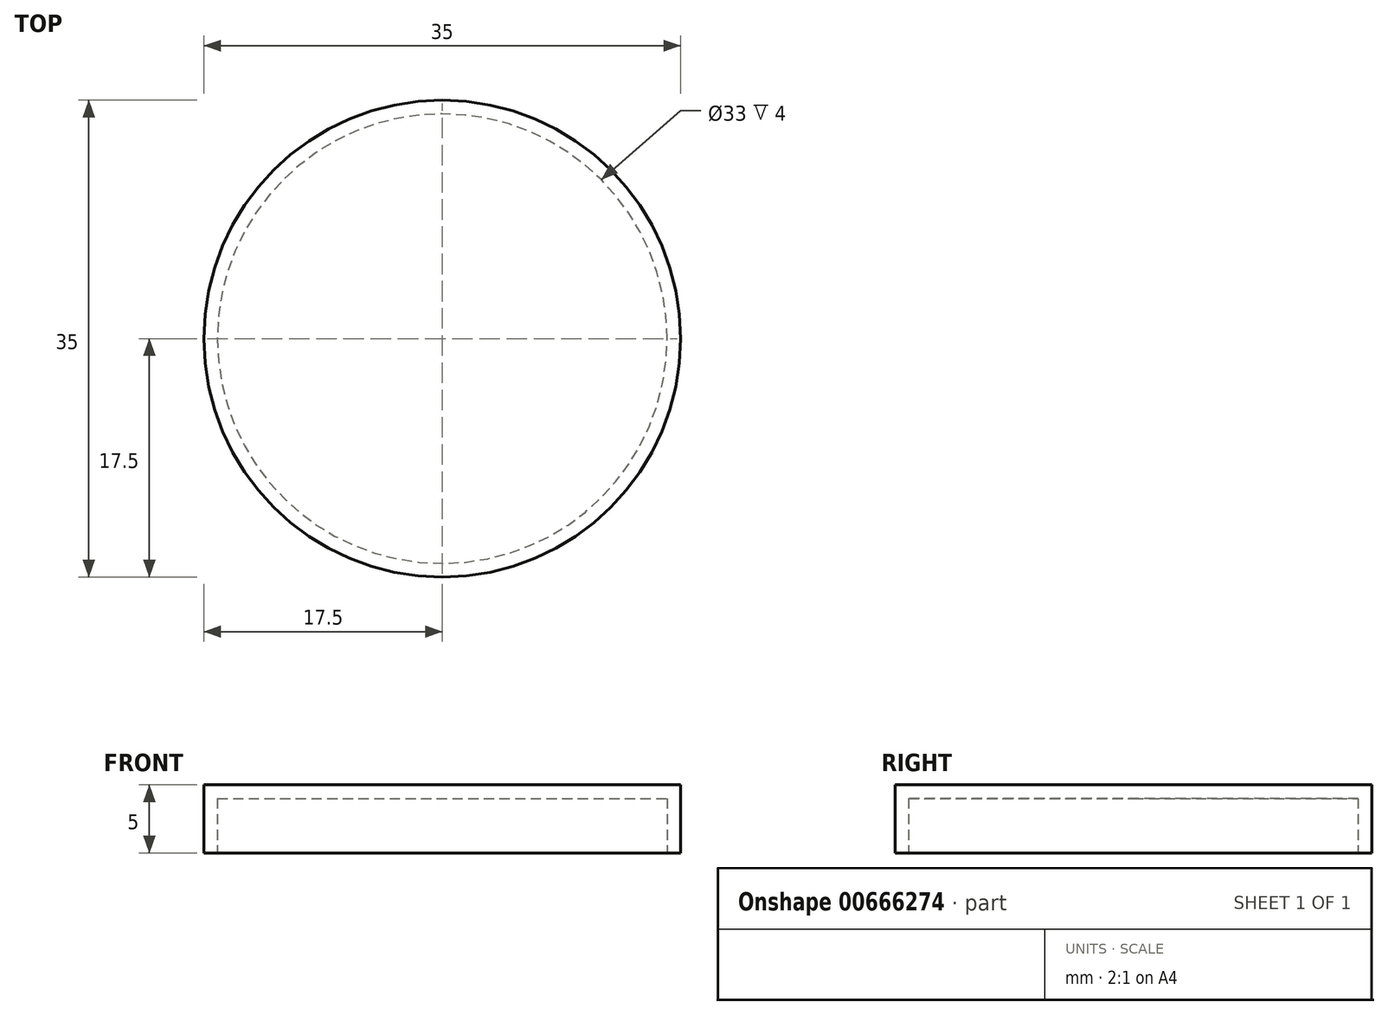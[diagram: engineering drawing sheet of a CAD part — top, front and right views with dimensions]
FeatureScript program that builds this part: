
annotation { "Feature Type Name" : "Feature", "Feature Type Description" : "" }
export const myFeature = defineFeature(function(context is Context, id is Id, definition is map)
    precondition{}
    {
        {
            var Q0;
            Q0=qCreatedBy(makeId("Front.planeOp"),FACE);
            var sketch = newSketch(context, id + "F0", { "sketchPlane" : qUnion([Q0])});
            skLineSegment(sketch, "E0", {"start": v(0, 0) * mm, "end": v(0, 56.8) * mm, "construction": true});
            skLineSegment(sketch, "E1", {"start": v(-4, 0) * mm, "end": v(-4, 12) * mm, "construction": true});
            skLineSegment(sketch, "E2", {"start": v(-4, 12) * mm, "end": v(-16.5, 12) * mm, "construction": true});
            skLineSegment(sketch, "E3", {"start": v(-16.5, 12) * mm, "end": v(-16.5, 39) * mm, "construction": true});
            skLineSegment(sketch, "E4", {"start": v(-16.5, 39) * mm, "end": v(0, 39) * mm});
            skLineSegment(sketch, "E5", {"start": v(0, 39) * mm, "end": v(0, 40) * mm});
            skLineSegment(sketch, "E6", {"start": v(0, 40) * mm, "end": v(-17.5, 40) * mm});
            skLineSegment(sketch, "E7", {"start": v(-17.5, 40) * mm, "end": v(-17.5, 11) * mm, "construction": true});
            skLineSegment(sketch, "E8", {"start": v(-17.5, 11) * mm, "end": v(-7, 11) * mm, "construction": true});
            skLineSegment(sketch, "E9", {"start": v(-7, 11) * mm, "end": v(-7, 0) * mm, "construction": true});
            skLineSegment(sketch, "E10", {"start": v(-7, 0) * mm, "end": v(-4, 0) * mm, "construction": true});
            skLineSegment(sketch, "E11", {"start": v(-16.5, 39) * mm, "end": v(-16.5, 35) * mm});
            skLineSegment(sketch, "E12", {"start": v(-16.5, 35) * mm, "end": v(-17.5, 35) * mm});
            skLineSegment(sketch, "E13", {"start": v(-17.5, 35) * mm, "end": v(-17.5, 40) * mm});
            skSolve(sketch);
        }
        {
            var Q0;
            Q0=qSketchRegion(id+"F0",true);
            var Q1;
            Q1=sQuery(id+"F0.wireOp",EDGE,"E0");
            revolve(context, id + "F1", {"surfaceOperationType" : NewSurfaceOperationType.NEW, "entities" : qUnion([Q0]), "axis" : qUnion([Q1]), "revolveType" : RevolveType.FULL});
        }
    });
